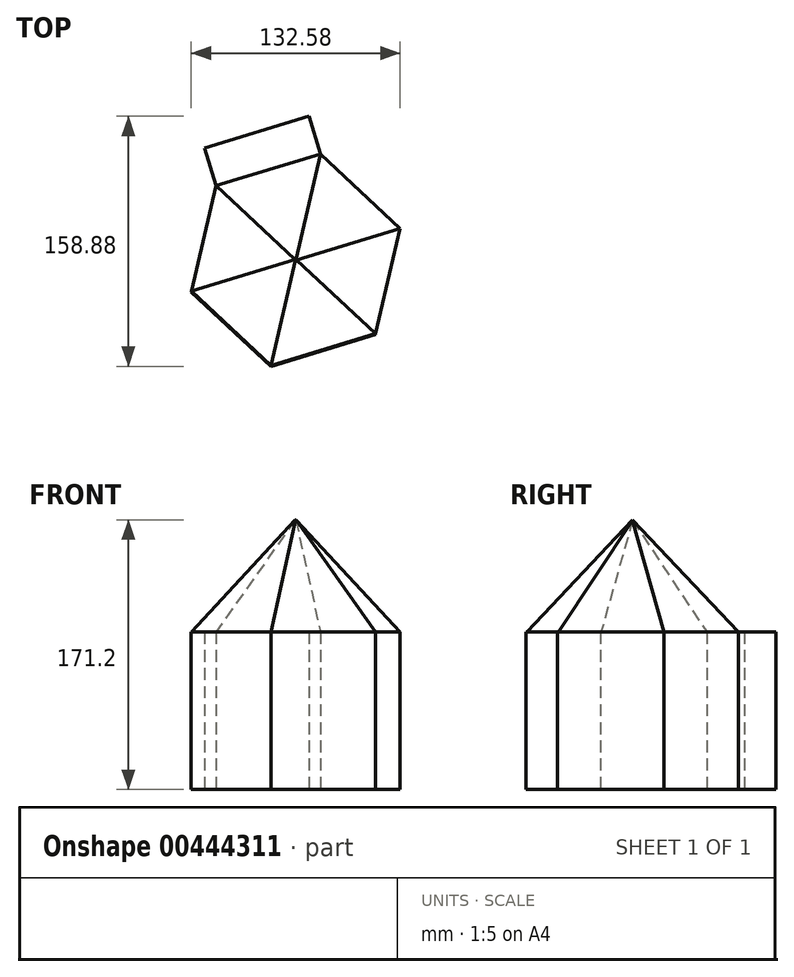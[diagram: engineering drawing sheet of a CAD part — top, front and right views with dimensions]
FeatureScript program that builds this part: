
annotation { "Feature Type Name" : "Feature", "Feature Type Description" : "" }
export const myFeature = defineFeature(function(context is Context, id is Id, definition is map)
    precondition{}
    {
        {
            var Q0;
            Q0=qCreatedBy(makeId("Top.planeOp"),FACE);
            var sketch = newSketch(context, id + "F0", { "sketchPlane" : qUnion([Q0])});
            skCircle(sketch, "E0.cCircle", {"center": v(0, -0.7) * mm, "radius": 60 * mm, "construction": true});
            skLineSegment(sketch, "E0.0", {"start": v(66.29, 19.44) * mm, "end": v(50.6, -48.04) * mm});
            skLineSegment(sketch, "E0.1", {"start": v(50.6, -48.04) * mm, "end": v(-15.7, -68.19) * mm});
            skLineSegment(sketch, "E0.2", {"start": v(-15.7, -68.19) * mm, "end": v(-66.29, -20.86) * mm});
            skLineSegment(sketch, "E0.3", {"start": v(-66.29, -20.86) * mm, "end": v(-50.6, 46.62) * mm});
            skLineSegment(sketch, "E0.4", {"start": v(-50.6, 46.62) * mm, "end": v(15.7, 66.77) * mm});
            skLineSegment(sketch, "E0.5", {"start": v(15.7, 66.77) * mm, "end": v(66.29, 19.44) * mm});
            skPoint(sketch, "E0.0.midPoint", {"position": v(58.44, -14.3) * mm});
            skSolve(sketch);
        }
        {
            var Q0;
            Q0=makeQuery(id+"F0.imprint","IMPRINT",FACE,{"disambiguationData":[TD([[makeQuery(id+"F0.imprint","IMPRINT",EDGE,{"derivedFrom":sQuery(id+"F0.wireOp",EDGE,"E0.0")}),-1.0]])]});
            extrude(context, id + "F1", {"entities" : qUnion([Q0]), "depth" : 100 * mm});
        }
        {
            var Q0;
            Q0=makeQuery(id+"F1.opExtrude","CAP_FACE",FACE,{"disambiguationData":[OSD([sQuery(id+"F0.wireOp",EDGE,"E0.0"),sQuery(id+"F0.wireOp",EDGE,"E0.1"),sQuery(id+"F0.wireOp",EDGE,"E0.2"),sQuery(id+"F0.wireOp",EDGE,"E0.3"),sQuery(id+"F0.wireOp",EDGE,"E0.4"),sQuery(id+"F0.wireOp",EDGE,"E0.5")])],"isStart":false});
            var sketch = newSketch(context, id + "F2", { "sketchPlane" : qUnion([Q0])});
            skCircle(sketch, "E1.cCircle", {"center": v(0, 0) * mm, "radius": 60.16 * mm, "construction": true});
            skLineSegment(sketch, "E1.0", {"start": v(66.46, 20.2) * mm, "end": v(50.73, -47.46) * mm});
            skLineSegment(sketch, "E1.1", {"start": v(50.73, -47.46) * mm, "end": v(-15.74, -67.66) * mm});
            skLineSegment(sketch, "E1.2", {"start": v(-15.74, -67.66) * mm, "end": v(-66.46, -20.2) * mm});
            skLineSegment(sketch, "E1.3", {"start": v(-66.46, -20.2) * mm, "end": v(-50.73, 47.46) * mm});
            skLineSegment(sketch, "E1.4", {"start": v(-50.73, 47.46) * mm, "end": v(15.74, 67.66) * mm});
            skLineSegment(sketch, "E1.5", {"start": v(15.74, 67.66) * mm, "end": v(66.46, 20.2) * mm});
            skPoint(sketch, "E1.0.midPoint", {"position": v(58.6, -13.63) * mm});
            skSolve(sketch);
        }
        {
            var Q0;
            {var subQ1=sQuery(id+"F2.wireOp",EDGE,"E1.1");Q0=makeQuery(id+"F2.imprint","IMPRINT",FACE,{"disambiguationData":[TD([[makeQuery(id+"F2.imprint","IMPRINT",EDGE,{"derivedFrom":subQ1}),-1.0]])]});}
            extrude(context, id + "F3", {"entities" : qUnion([Q0]), "operationType" : NewBodyOperationType.ADD, "depth" : 80 * mm, "hasDraft" : true, "draftAngle" : 40 * degree, "draftPullDirection" : true});
        }
        {
            var Q0;
            Q0=makeQuery(id+"F1.opExtrude","SWEPT_FACE",FACE,{"disambiguationData":[OSD([sQuery(id+"F0.wireOp",EDGE,"E0.4")])]});
            var sketch = newSketch(context, id + "F4", { "sketchPlane" : qUnion([Q0])});
            skLineSegment(sketch, "E2.bottom", {"start": v(-34.44, 100) * mm, "end": v(34.85, 100) * mm});
            skLineSegment(sketch, "E2.top", {"start": v(-34.44, 0) * mm, "end": v(34.85, 0) * mm});
            skLineSegment(sketch, "E2.left", {"start": v(-34.44, 100) * mm, "end": v(-34.44, 0) * mm});
            skLineSegment(sketch, "E2.right", {"start": v(34.85, 100) * mm, "end": v(34.85, 0) * mm});
            skSolve(sketch);
        }
        {
            var Q0;
            Q0 = qSketchRegion(id + "F4", true);
            extrude(context, id + "F5", {"entities" : qUnion([Q0]), "operationType" : NewBodyOperationType.ADD, "depth" : 25 * mm});
        }
    });
